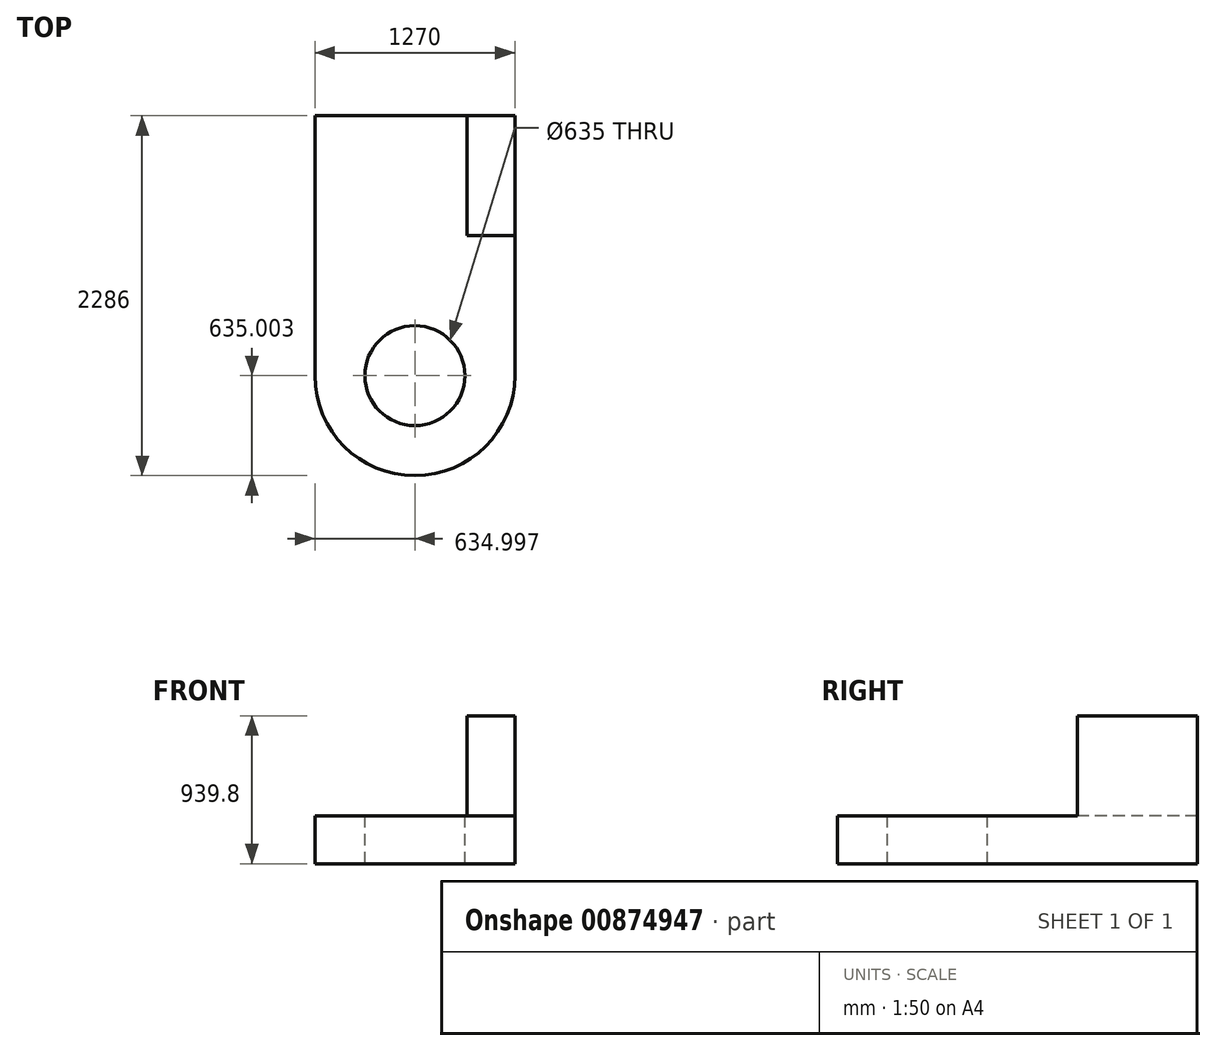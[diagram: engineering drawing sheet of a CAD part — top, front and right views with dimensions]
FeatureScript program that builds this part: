
annotation { "Feature Type Name" : "Feature", "Feature Type Description" : "" }
export const myFeature = defineFeature(function(context is Context, id is Id, definition is map)
    precondition{}
    {
        {
            var Q0;
            Q0=qCreatedBy(makeId("Top.planeOp"),FACE);
            var sketch = newSketch(context, id + "F0", { "sketchPlane" : qUnion([Q0])});
            skLineSegment(sketch, "E0", {"start": v(-33.84, 1647.3) * mm, "end": v(-33.84, -3.7) * mm});
            skLineSegment(sketch, "E1", {"start": v(-33.84, 1647.3) * mm, "end": v(1236.16, 1647.3) * mm});
            skLineSegment(sketch, "E2", {"start": v(1236.16, 1647.3) * mm, "end": v(1236.16, -3.7) * mm});
            skLineSegment(sketch, "E3", {"start": v(1236.16, -3.7) * mm, "end": v(-33.84, -3.7) * mm});
            skSolve(sketch);
        }
        {
            var Q0;
            Q0=makeQuery(id+"F0.imprint","IMPRINT",FACE,{"disambiguationData":[TD([[makeQuery(id+"F0.imprint","IMPRINT",EDGE,{"derivedFrom":sQuery(id+"F0.wireOp",EDGE,"E0")}),1.0]])]});
            extrude(context, id + "F1", {"entities" : qUnion([Q0]), "depth" : 304.8 * mm, "offsetDistance" : 25.4 * mm});
        }
        {
            var Q0;
            Q0=makeQuery(id+"F1.opExtrude","CAP_FACE",FACE,{"disambiguationData":[OSD([sQuery(id+"F0.wireOp",EDGE,"E0"),sQuery(id+"F0.wireOp",EDGE,"E1"),sQuery(id+"F0.wireOp",EDGE,"E2"),sQuery(id+"F0.wireOp",EDGE,"E3")])],"isStart":false});
            var sketch = newSketch(context, id + "F2", { "sketchPlane" : qUnion([Q0])});
            skLineSegment(sketch, "E4", {"start": v(1236.16, 1647.3) * mm, "end": v(931.36, 1647.3) * mm});
            skLineSegment(sketch, "E5", {"start": v(931.36, 1647.3) * mm, "end": v(931.36, 885.3) * mm});
            skLineSegment(sketch, "E6", {"start": v(931.36, 885.3) * mm, "end": v(1236.16, 885.3) * mm});
            skLineSegment(sketch, "E7", {"start": v(1236.16, 885.3) * mm, "end": v(1236.16, 1647.3) * mm});
            skSolve(sketch);
        }
        {
            var Q0;
            Q0=makeQuery(id+"F2.imprint","IMPRINT",FACE,{"disambiguationData":[TD([[makeQuery(id+"F2.imprint","IMPRINT",EDGE,{"derivedFrom":sQuery(id+"F2.wireOp",EDGE,"E4")}),-1.0]])]});
            extrude(context, id + "F3", {"entities" : qUnion([Q0]), "operationType" : NewBodyOperationType.ADD, "depth" : 635 * mm, "offsetDistance" : 25.4 * mm});
        }
        {
            var Q0;
            Q0=makeQuery(id+"F1.opExtrude","CAP_FACE",FACE,{"disambiguationData":[OSD([sQuery(id+"F0.wireOp",EDGE,"E0"),sQuery(id+"F0.wireOp",EDGE,"E1"),sQuery(id+"F0.wireOp",EDGE,"E2"),sQuery(id+"F0.wireOp",EDGE,"E3")])],"isStart":false});
            var sketch = newSketch(context, id + "F4", { "sketchPlane" : qUnion([Q0])});
            skCircle(sketch, "E8", {"center": v(601.16, -3.7) * mm, "radius": 635 * mm});
            skSolve(sketch);
        }
        {
            var Q0;
            {var subQ1=makeQuery(id+"F1.opExtrude","CAP_EDGE",EDGE,{"disambiguationData":[OSD([sQuery(id+"F0.wireOp",EDGE,"E3")])],"isStart":false});Q0=makeQuery(id+"F4.imprint","IMPRINT",FACE,{"disambiguationData":[TD([[makeQuery(id+"F4.imprint","IMPRINT",EDGE,{"derivedFrom":subQ1}),1.0]])]});}
            extrude(context, id + "F5", {"entities" : qUnion([Q0]), "operationType" : NewBodyOperationType.ADD, "oppositeDirection" : true, "depth" : 304.8 * mm, "offsetDistance" : 25.4 * mm});
        }
        {
            var Q0;
            {var subQ0=sQuery(id+"F0.wireOp",EDGE,"E3");Q0=makeQuery(id+"F5.boolean.opBoolean","MERGE",FACE,{"derivedFrom":[makeQuery(id+"F1.opExtrude","CAP_FACE",FACE,{"disambiguationData":[OSD([sQuery(id+"F0.wireOp",EDGE,"E0"),sQuery(id+"F0.wireOp",EDGE,"E1"),sQuery(id+"F0.wireOp",EDGE,"E2"),subQ0])],"isStart":false}),makeQuery(id+"F5.opExtrude","CAP_FACE",FACE,{"disambiguationData":[OSD([subQ0,sQuery(id+"F4.wireOp",EDGE,"E8")])],"isStart":true})]});}
            var sketch = newSketch(context, id + "F6", { "sketchPlane" : qUnion([Q0])});
            skCircle(sketch, "E9", {"center": v(601.16, -3.7) * mm, "radius": 317.5 * mm});
            skSolve(sketch);
        }
        {
            var Q0;
            Q0=makeQuery(id+"F6.imprint","IMPRINT",FACE,{"disambiguationData":[TD([[makeQuery(id+"F6.imprint","IMPRINT",EDGE,{"derivedFrom":sQuery(id+"F6.wireOp",EDGE,"E9")}),1.0]])]});
            extrude(context, id + "F7", {"entities" : qUnion([Q0]), "operationType" : NewBodyOperationType.REMOVE, "oppositeDirection" : true, "depth" : 304.8 * mm, "offsetDistance" : 25.4 * mm});
        }
    });
